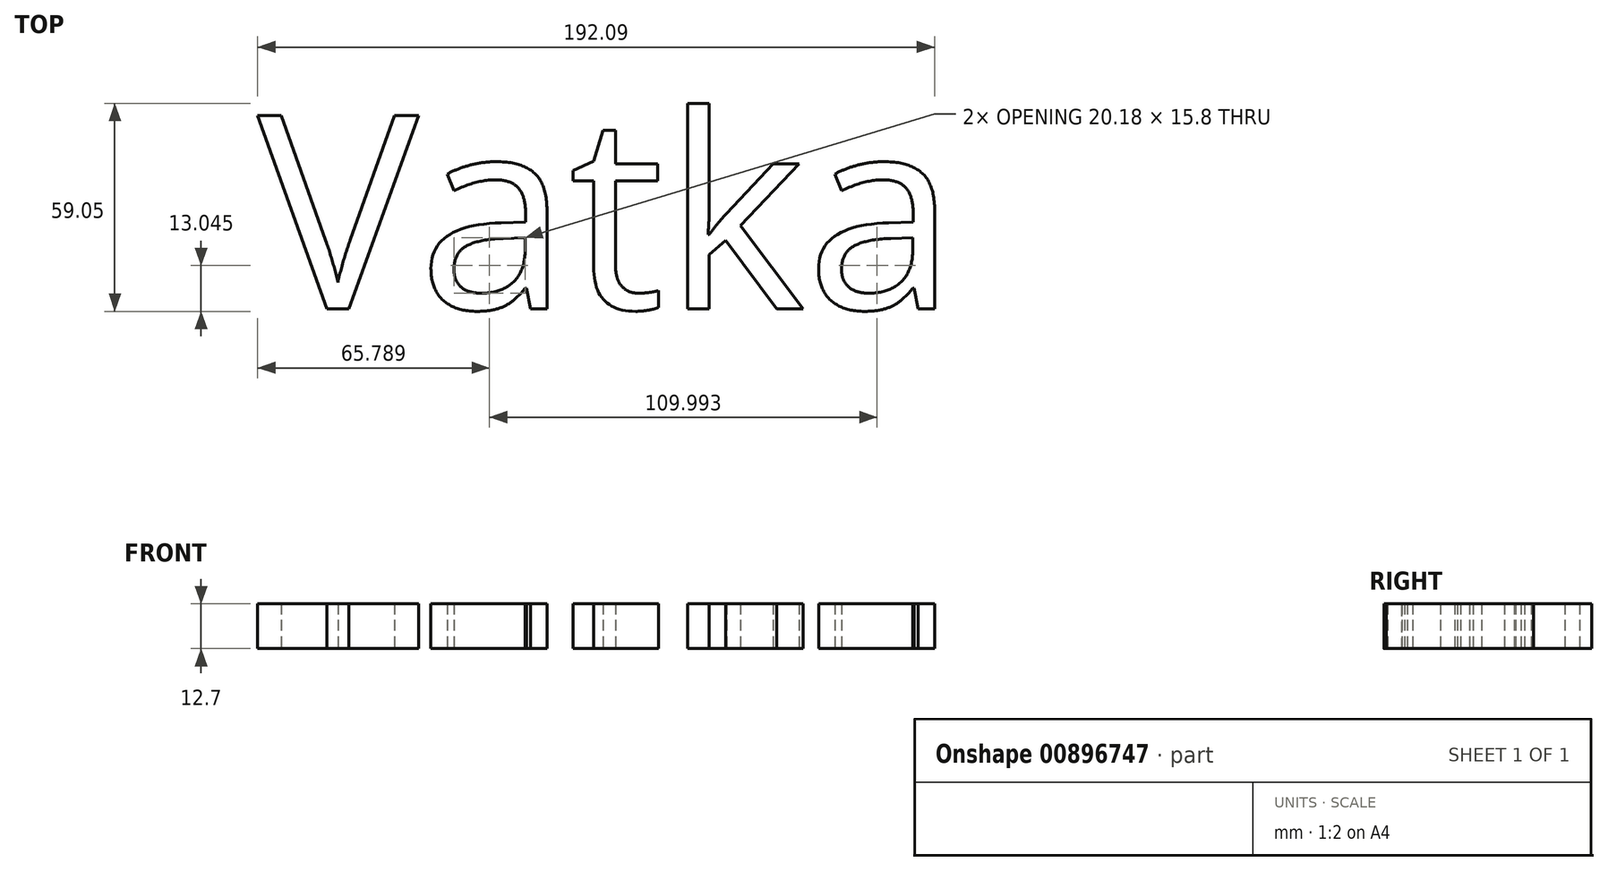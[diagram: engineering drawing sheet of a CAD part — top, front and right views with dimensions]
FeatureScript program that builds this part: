
annotation { "Feature Type Name" : "Feature", "Feature Type Description" : "" }
export const myFeature = defineFeature(function(context is Context, id is Id, definition is map)
    precondition{}
    {
        {
            var Q0;
            Q0=qCreatedBy(makeId("Top.planeOp"),FACE);
            var sketch = newSketch(context, id + "F0", { "sketchPlane" : qUnion([Q0])});
            skText(sketch, "E0", { "text": "Vatka ", "fontName": "OpenSans-Regular.ttf"});
            const initialGuessF0  = {"E0": [-0.0737, -0.02083, 1, 0, 0.05523]};
            skSetInitialGuess(sketch, initialGuessF0);
            skSolve(sketch);
        }
        {
            var Q0;
            Q0 = qSketchRegion(id + "F0", true);
            extrude(context, id + "F1", {"entities" : qUnion([Q0]), "depth" : 12.7 * mm, "offsetDistance" : 25.4 * mm});
        }
    });
